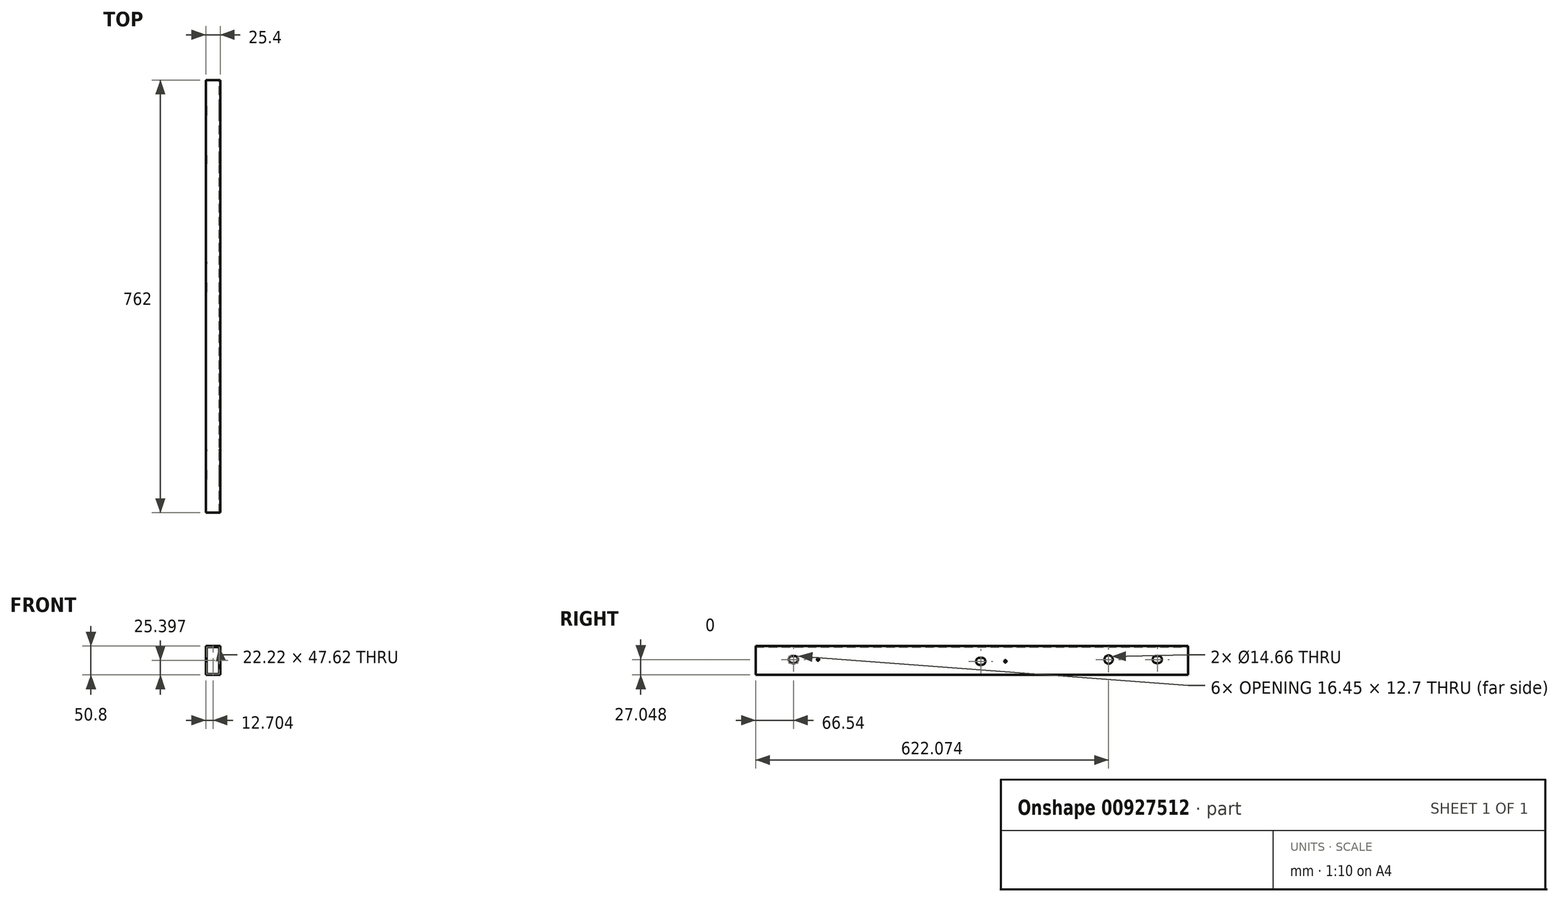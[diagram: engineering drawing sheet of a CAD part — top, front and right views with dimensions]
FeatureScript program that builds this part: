
annotation { "Feature Type Name" : "Feature", "Feature Type Description" : "" }
export const myFeature = defineFeature(function(context is Context, id is Id, definition is map)
    precondition{}
    {
        {
            var Q0;
            Q0=qCreatedBy(makeId("Front.planeOp"),FACE);
            var sketch = newSketch(context, id + "F0", { "sketchPlane" : qUnion([Q0])});
            skLineSegment(sketch, "E0.bottom", {"start": v(2.18, 50.27) * mm, "end": v(27.58, 50.27) * mm});
            skLineSegment(sketch, "E0.top", {"start": v(2.18, -0.53) * mm, "end": v(27.58, -0.53) * mm});
            skLineSegment(sketch, "E0.left", {"start": v(2.18, 50.27) * mm, "end": v(2.18, -0.53) * mm});
            skLineSegment(sketch, "E0.right", {"start": v(27.58, 50.27) * mm, "end": v(27.58, -0.53) * mm});
            skLineSegment(sketch, "E1.bottom", {"start": v(3.77, 48.68) * mm, "end": v(26, 48.68) * mm});
            skLineSegment(sketch, "E1.top", {"start": v(3.77, 1.05) * mm, "end": v(26, 1.05) * mm});
            skLineSegment(sketch, "E1.left", {"start": v(3.77, 48.68) * mm, "end": v(3.77, 1.05) * mm});
            skLineSegment(sketch, "E1.right", {"start": v(26, 48.68) * mm, "end": v(26, 1.05) * mm});
            skSolve(sketch);
        }
        {
            var Q0;
            Q0=makeQuery(id+"F0.imprint","IMPRINT",FACE,{"disambiguationData":[TD([[makeQuery(id+"F0.imprint","IMPRINT",EDGE,{"derivedFrom":sQuery(id+"F0.wireOp",EDGE,"E0.bottom")}),-1.0]])]});
            extrude(context, id + "F1", {"entities" : qUnion([Q0]), "depth" : 762 * mm, "offsetDistance" : 25.4 * mm});
        }
        {
            var Q0;
            Q0=makeQuery(id+"F1.opExtrude","SWEPT_FACE",FACE,{"disambiguationData":[OSD([sQuery(id+"F0.wireOp",EDGE,"E0.right")])]});
            var sketch = newSketch(context, id + "F2", { "sketchPlane" : qUnion([Q0])});
            skLineSegment(sketch, "E2", {"start": v(-695.55, 26.52) * mm, "end": v(-730.25, 26.52) * mm});
            skLineSegment(sketch, "E3", {"start": v(-695.55, 20.17) * mm, "end": v(-695.55, 20.17) * mm});
            skArc(sketch, "E4", {"start": v(-693.59, 20.17) * mm, "mid": v(-687.24, 26.53) * mm, "end": v(-693.61, 32.87) * mm});
            skArc(sketch, "E5", {"start": v(-697.3, 32.87) * mm, "mid": v(-703.68, 26.53) * mm, "end": v(-697.33, 20.17) * mm});
            skLineSegment(sketch, "E6", {"start": v(-697.36, 32.87) * mm, "end": v(-693.56, 32.87) * mm});
            skLineSegment(sketch, "E7", {"start": v(-693.59, 20.17) * mm, "end": v(-697.33, 20.17) * mm});
            skArc(sketch, "E8.trimOffspring", {"start": v(-695.53, 32.87) * mm, "mid": v(-695.55, 32.87) * mm, "end": v(-695.58, 32.87) * mm});
            skArc(sketch, "E9", {"start": v(-363.39, 17) * mm, "mid": v(-357.04, 23.36) * mm, "end": v(-363.41, 29.7) * mm});
            skArc(sketch, "E10", {"start": v(-367.1, 29.7) * mm, "mid": v(-373.48, 23.36) * mm, "end": v(-367.13, 17) * mm});
            skLineSegment(sketch, "E11", {"start": v(-367.16, 29.7) * mm, "end": v(-363.36, 29.7) * mm});
            skLineSegment(sketch, "E12", {"start": v(-363.39, 17) * mm, "end": v(-367.13, 17) * mm});
            skArc(sketch, "E13.trimOffspring", {"start": v(-365.33, 29.7) * mm, "mid": v(-365.35, 29.7) * mm, "end": v(-365.38, 29.7) * mm});
            skLineSegment(sketch, "E14", {"start": v(-54.22, 20.17) * mm, "end": v(-54.22, 20.17) * mm});
            skArc(sketch, "E15", {"start": v(-52.25, 20.17) * mm, "mid": v(-45.9, 26.53) * mm, "end": v(-52.28, 32.87) * mm});
            skArc(sketch, "E16", {"start": v(-55.97, 32.87) * mm, "mid": v(-62.35, 26.53) * mm, "end": v(-56, 20.17) * mm});
            skLineSegment(sketch, "E17", {"start": v(-56.03, 32.87) * mm, "end": v(-52.23, 32.87) * mm});
            skLineSegment(sketch, "E18", {"start": v(-52.25, 20.17) * mm, "end": v(-56, 20.17) * mm});
            skArc(sketch, "E19.trimOffspring", {"start": v(-54.2, 32.87) * mm, "mid": v(-54.22, 32.87) * mm, "end": v(-54.24, 32.87) * mm});
            skCircle(sketch, "E20", {"center": v(-321.87, 23.34) * mm, "radius": 2 * mm});
            skCircle(sketch, "E21", {"center": v(-652.07, 26.52) * mm, "radius": 2 * mm});
            skCircle(sketch, "E22", {"center": v(-139.93, 26.52) * mm, "radius": 7.33 * mm});
            skSolve(sketch);
        }
        {
            var Q0;
            Q0 = qSketchRegion(id + "F2", true);
            extrude(context, id + "F3", {"entities" : qUnion([Q0]), "operationType" : NewBodyOperationType.REMOVE, "endBound" : BoundingType.THROUGH_ALL, "oppositeDirection" : true, "depth" : 25.4 * mm, "offsetDistance" : 25.4 * mm});
        }
    });
